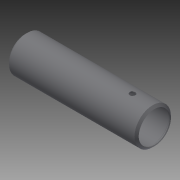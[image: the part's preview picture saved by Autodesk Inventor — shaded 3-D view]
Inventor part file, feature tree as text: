
AUTODESK INVENTOR PART (.ipt)
format: ipt  version: 2014 (Build 180170000, 170)  size: 139,264 bytes
history: native  units: in
note: dims shown in document units (in); Inventor stores cm internally (conversion verified against a paired STEP export)
features: other x56, revolve x2, sketch x2
ambient origin geometry x8: Origin, YZ Plane, XZ Plane, XY Plane, X Axis, Y Axis, Z Axis, Center Point
bodies: Solid1 (feature_tree)
feature tree (60):
  revolve  "Revolution1"  Angle=360.0deg
  revolve  "Revolution2"  [1 undecoded]
  other  "o1_XY"
  other  "o1_YZ"
  other  "o1_ZX"
  other  "o1_X"
  other  "o1_Y"
  other  "o1_Z"
  other  "o1_Center"
  other  "o2_XY"
  other  "o2_YZ"
  other  "o2_ZX"
  other  "o2_X"
  other  "o2_Y"
  other  "o2_Z"
  other  "o2_Center"
  other  "t1_XY"
  other  "t1_YZ"
  other  "t1_ZX"
  other  "t1_X"
  other  "t1_Y"
  other  "t1_Z"
  other  "t1_Center"
  other  "t2_XY"
  other  "t2_YZ"
  other  "t2_ZX"
  other  "t2_X"
  other  "t2_Y"
  other  "t2_Z"
  other  "t2_Center"
  other  "t3_XY"
  other  "t3_YZ"
  other  "t3_ZX"
  other  "t3_X"
  other  "t3_Y"
  other  "t3_Z"
  other  "t3_Center"
  other  "t4_XY"
  other  "t4_YZ"
  other  "t4_ZX"
  other  "t4_X"
  other  "t4_Y"
  other  "t4_Z"
  other  "t4_Center"
  other  "tube1_XY"
  other  "tube1_YZ"
  other  "tube1_ZX"
  other  "tube1_X"
  other  "tube1_Y"
  other  "tube1_Z"
  other  "tube1_Center"
  other  "tube2_XY"
  other  "tube2_YZ"
  other  "tube2_ZX"
  other  "tube2_X"
  other  "tube2_Y"
  other  "tube2_Z"
  other  "tube2_Center"
  sketch  "Sketch_5"
  sketch  "Sketch_1"  dims[d0=360.0deg d1=360.0deg]
note: 1 required parameter value undecoded (feature->parameter linkage not recoverable at this tier; creation-order binding heuristic only, values carry confidence <= 0.55)
